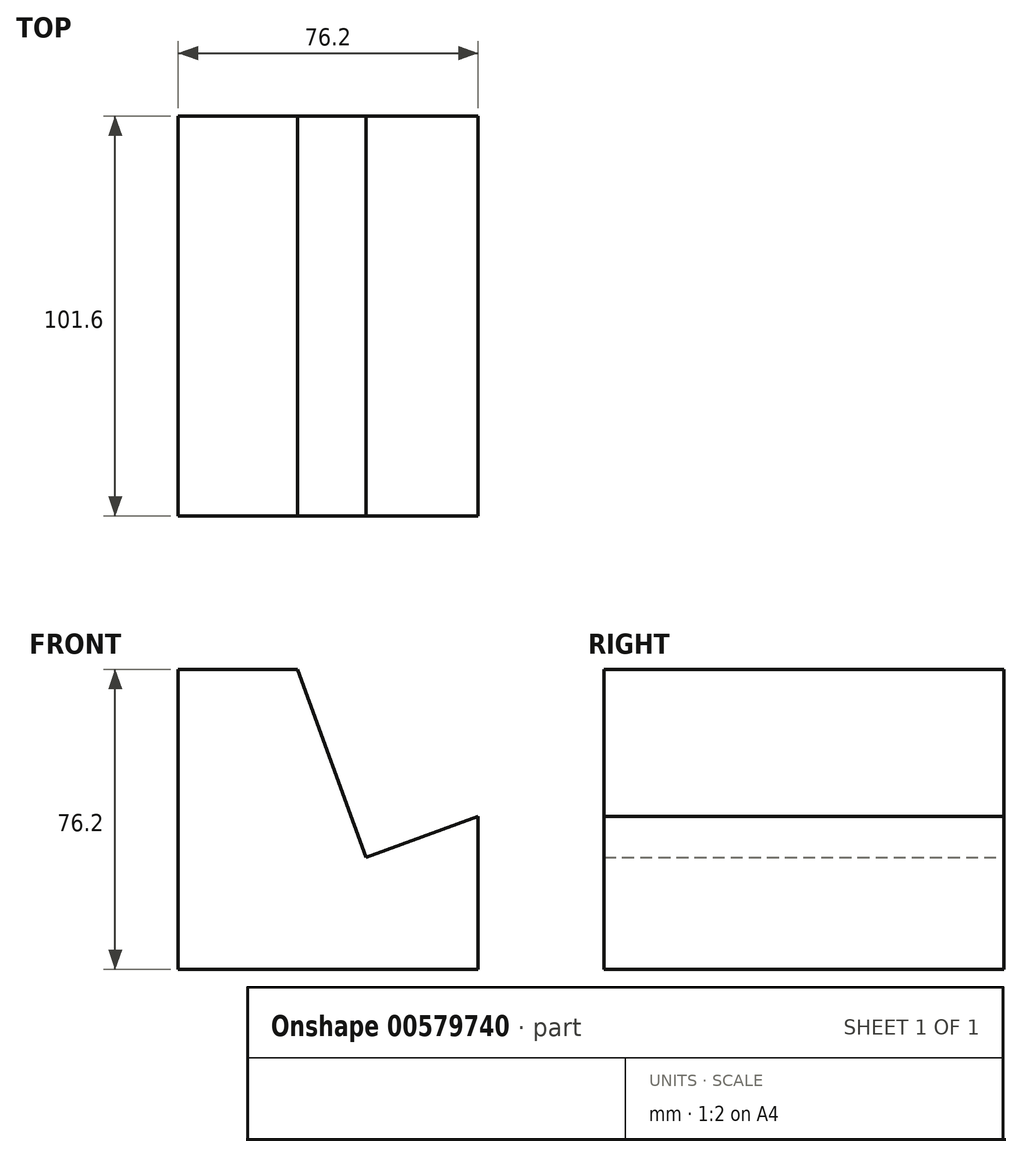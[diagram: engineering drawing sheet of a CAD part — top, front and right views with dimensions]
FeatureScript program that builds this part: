
annotation { "Feature Type Name" : "Feature", "Feature Type Description" : "" }
export const myFeature = defineFeature(function(context is Context, id is Id, definition is map)
    precondition{}
    {
        {
            var Q0;
            Q0=qCreatedBy(makeId("Front.planeOp"),FACE);
            var sketch = newSketch(context, id + "F0", { "sketchPlane" : qUnion([Q0])});
            skLineSegment(sketch, "E0.bottom", {"start": v(0, 76.2) * mm, "end": v(30.33, 76.2) * mm});
            skLineSegment(sketch, "E0.top", {"start": v(0, 0) * mm, "end": v(76.2, 0) * mm});
            skLineSegment(sketch, "E0.left", {"start": v(0, 76.2) * mm, "end": v(0, 0) * mm});
            skLineSegment(sketch, "E0.right", {"start": v(76.2, 38.84) * mm, "end": v(76.2, 0) * mm});
            skLineSegment(sketch, "E1", {"start": v(30.33, 76.2) * mm, "end": v(47.7, 28.46) * mm});
            skLineSegment(sketch, "E2", {"start": v(47.7, 28.46) * mm, "end": v(76.2, 38.84) * mm});
            skSolve(sketch);
        }
        {
            var Q0;
            Q0=makeQuery(id+"F0.imprint","IMPRINT",FACE,{"disambiguationData":[TD([[makeQuery(id+"F0.imprint","IMPRINT",EDGE,{"derivedFrom":sQuery(id+"F0.wireOp",EDGE,"E0.bottom")}),-1.0]])]});
            extrude(context, id + "F1", {"entities" : qUnion([Q0]), "depth" : 101.6 * mm, "offsetDistance" : 25.4 * mm});
        }
    });
